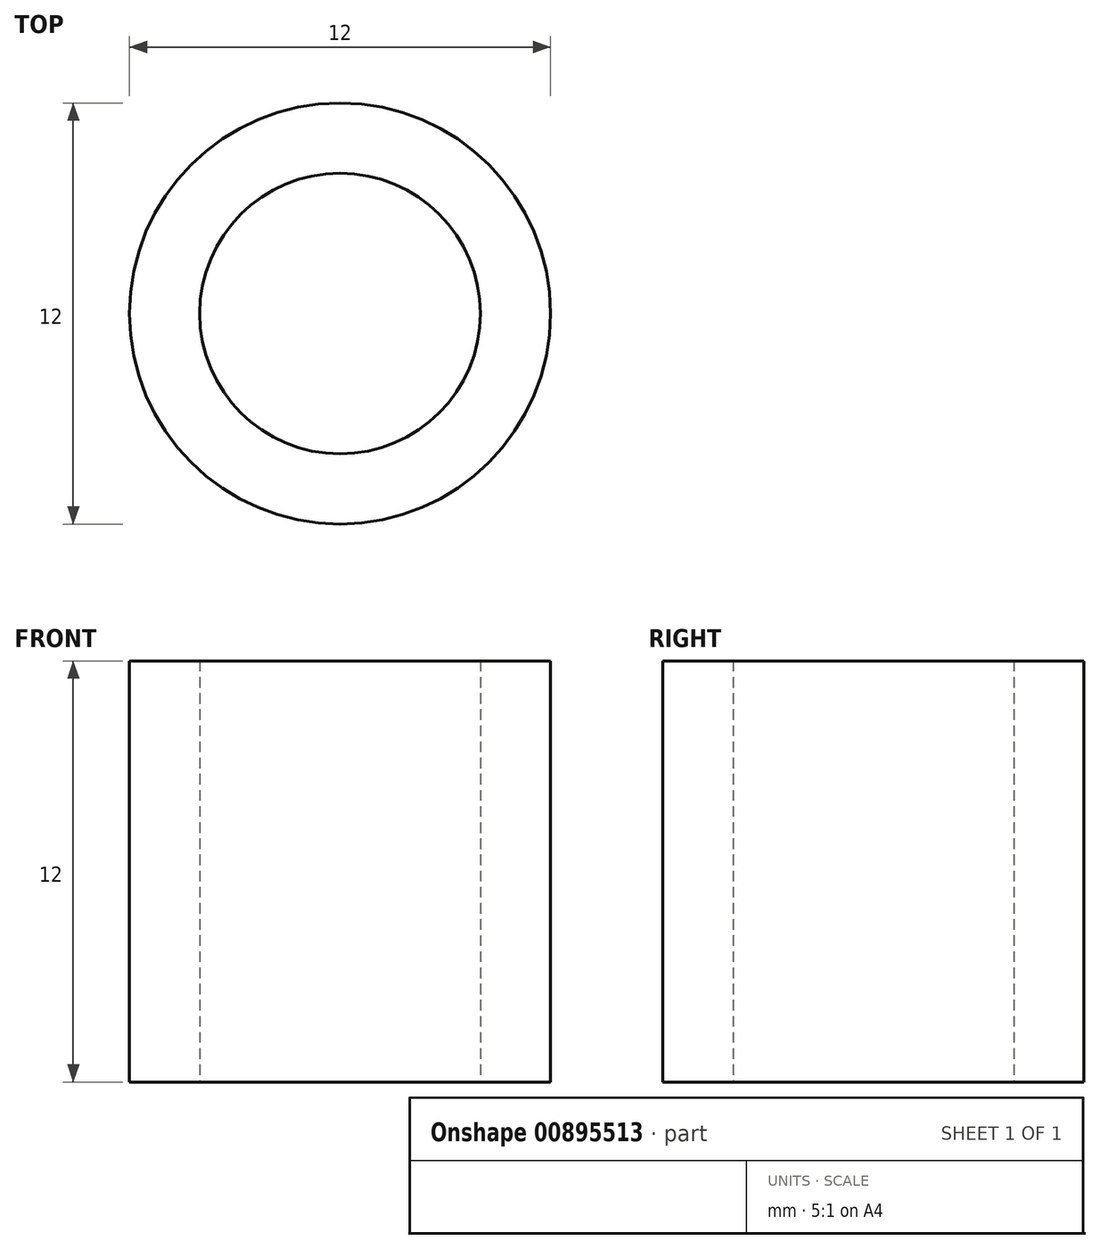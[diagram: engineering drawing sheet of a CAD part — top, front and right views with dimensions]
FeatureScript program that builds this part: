
annotation { "Feature Type Name" : "Feature", "Feature Type Description" : "" }
export const myFeature = defineFeature(function(context is Context, id is Id, definition is map)
    precondition{}
    {
        {
            var Q0;
            Q0=qCreatedBy(makeId("Top.planeOp"),FACE);
            var sketch = newSketch(context, id + "F0", { "sketchPlane" : qUnion([Q0])});
            skCircle(sketch, "E0", {"center": v(0, 0) * mm, "radius": 4 * mm});
            skCircle(sketch, "E1", {"center": v(0, 0) * mm, "radius": 6 * mm});
            skSolve(sketch);
        }
        {
            var Q0;
            Q0 = qSketchRegion(id + "F0", true);
            extrude(context, id + "F1", {"entities" : qUnion([Q0]), "depth" : 12 * mm, "offsetDistance" : 25 * mm});
        }
    });
